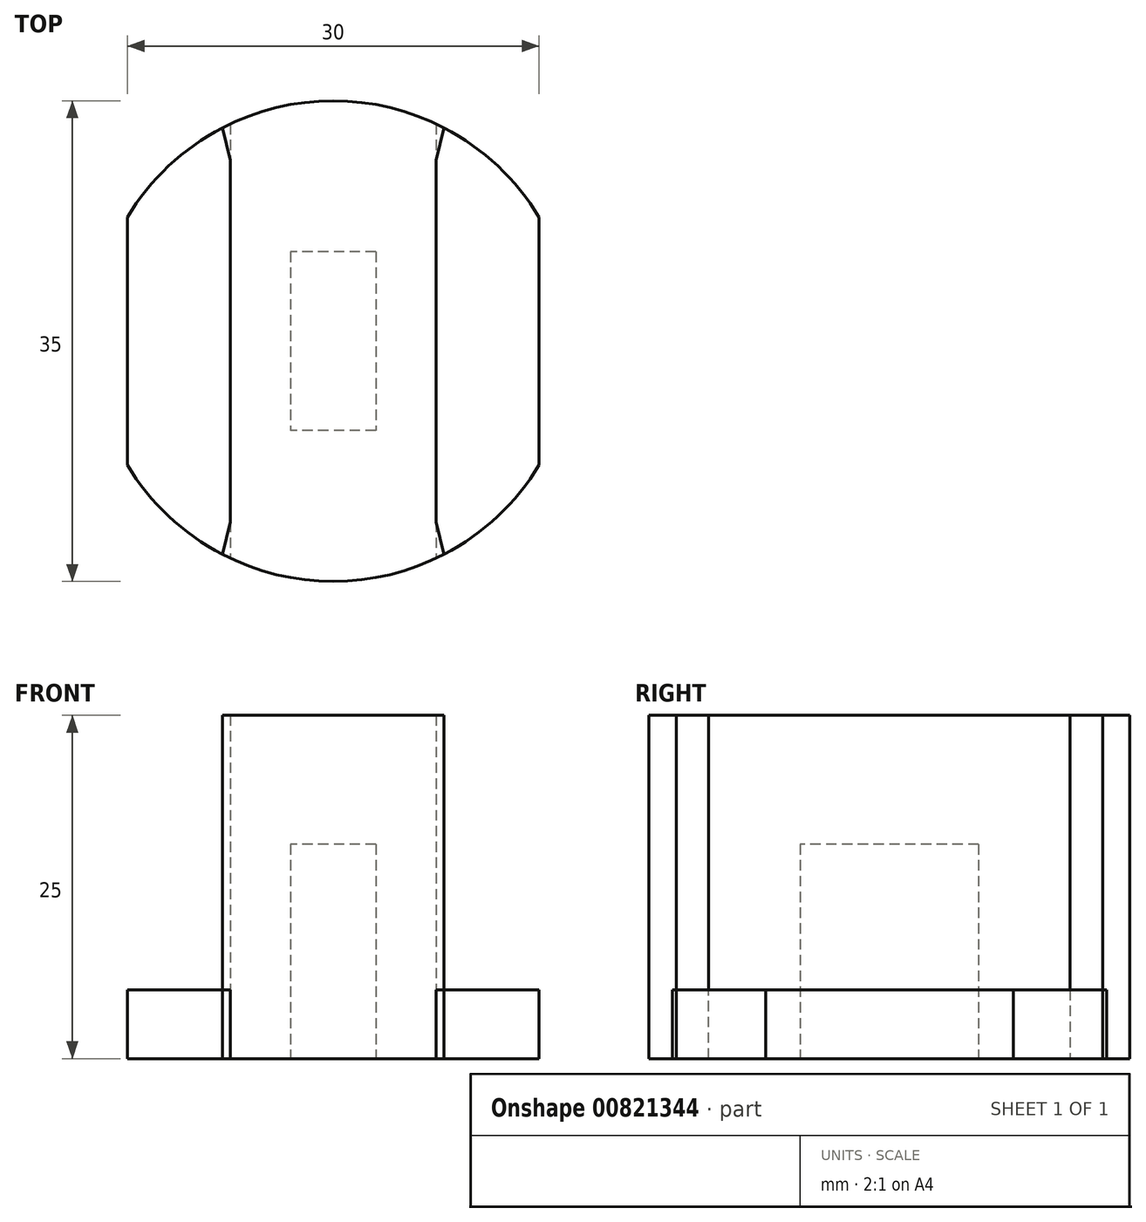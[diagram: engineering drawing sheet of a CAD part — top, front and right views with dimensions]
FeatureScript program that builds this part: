
annotation { "Feature Type Name" : "Feature", "Feature Type Description" : "" }
export const myFeature = defineFeature(function(context is Context, id is Id, definition is map)
    precondition{}
    {
        {
            var Q0;
            Q0=qCreatedBy(makeId("Top.planeOp"),FACE);
            var sketch = newSketch(context, id + "F0", { "sketchPlane" : qUnion([Q0])});
            skCircle(sketch, "E0", {"center": v(0, 0) * mm, "radius": 17.5 * mm});
            skLineSegment(sketch, "E1.bottom", {"start": v(7.5, 20) * mm, "end": v(-7.5, 20) * mm});
            skLineSegment(sketch, "E1.top", {"start": v(7.5, -20) * mm, "end": v(-7.5, -20) * mm});
            skLineSegment(sketch, "E1.left", {"start": v(7.5, 20) * mm, "end": v(7.5, -20) * mm});
            skLineSegment(sketch, "E1.right", {"start": v(-7.5, 20) * mm, "end": v(-7.5, -20) * mm});
            skLineSegment(sketch, "E2.bottom", {"start": v(3.1, 6.5) * mm, "end": v(-3.1, 6.5) * mm});
            skLineSegment(sketch, "E2.top", {"start": v(3.1, -6.5) * mm, "end": v(-3.1, -6.5) * mm});
            skLineSegment(sketch, "E2.left", {"start": v(3.1, 6.5) * mm, "end": v(3.1, -6.5) * mm});
            skLineSegment(sketch, "E2.right", {"start": v(-3.1, 6.5) * mm, "end": v(-3.1, -6.5) * mm});
            skLineSegment(sketch, "E3.bottom", {"start": v(15, 20) * mm, "end": v(-15, 20) * mm});
            skLineSegment(sketch, "E3.top", {"start": v(15, -20) * mm, "end": v(-15, -20) * mm});
            skLineSegment(sketch, "E3.left", {"start": v(15, 20) * mm, "end": v(15, -20) * mm});
            skLineSegment(sketch, "E3.right", {"start": v(-15, 20) * mm, "end": v(-15, -20) * mm});
            skLineSegment(sketch, "E4.bottom", {"start": v(23.86, 11.75) * mm, "end": v(-23.86, 11.75) * mm});
            skLineSegment(sketch, "E4.top", {"start": v(23.86, -11.75) * mm, "end": v(-23.86, -11.75) * mm});
            skLineSegment(sketch, "E4.left", {"start": v(23.86, 11.75) * mm, "end": v(23.86, -11.75) * mm});
            skLineSegment(sketch, "E4.right", {"start": v(-23.86, 11.75) * mm, "end": v(-23.86, -11.75) * mm});
            skSolve(sketch);
        }
        {
            var Q0;
            {var subQ0=sQuery(id+"F0.wireOp",EDGE,"E3.left");var subQ1=sQuery(id+"F0.wireOp",EDGE,"E0");var subQ2=makeQuery(id+"F0.imprint","INTERSECT",VERTEX,{"disambiguationData":[OD(0.0)],"derivedFrom":[subQ1,subQ0]});Q0=makeQuery(id+"F0.imprint","IMPRINT",FACE,{"disambiguationData":[TD([[makeQuery(id+"F0.imprint","IMPRINT",EDGE,{"disambiguationData":[TD([[subQ2,-1.0]])],"derivedFrom":subQ1}),1.0]])]});}
            var Q1;
            {var subQ0=sQuery(id+"F0.wireOp",EDGE,"E3.right");var subQ1=sQuery(id+"F0.wireOp",EDGE,"E0");var subQ2=makeQuery(id+"F0.imprint","INTERSECT",VERTEX,{"disambiguationData":[OD(0.0)],"derivedFrom":[subQ1,subQ0]});Q1=makeQuery(id+"F0.imprint","IMPRINT",FACE,{"disambiguationData":[TD([[makeQuery(id+"F0.imprint","IMPRINT",EDGE,{"disambiguationData":[TD([[subQ2,1.0]])],"derivedFrom":subQ1}),1.0]])]});}
            var Q2;
            {var subQ0=sQuery(id+"F0.wireOp",EDGE,"E1.right");var subQ1=sQuery(id+"F0.wireOp",EDGE,"E0");var subQ2=makeQuery(id+"F0.imprint","INTERSECT",VERTEX,{"disambiguationData":[OD(0.0)],"derivedFrom":[subQ1,subQ0]});Q2=makeQuery(id+"F0.imprint","IMPRINT",FACE,{"disambiguationData":[TD([[makeQuery(id+"F0.imprint","IMPRINT",EDGE,{"disambiguationData":[TD([[subQ2,-1.0]])],"derivedFrom":subQ1}),1.0]])]});}
            var Q3;
            {var subQ0=sQuery(id+"F0.wireOp",EDGE,"E1.left");var subQ1=sQuery(id+"F0.wireOp",EDGE,"E0");var subQ2=makeQuery(id+"F0.imprint","INTERSECT",VERTEX,{"disambiguationData":[OD(1.0)],"derivedFrom":[subQ1,subQ0]});Q3=makeQuery(id+"F0.imprint","IMPRINT",FACE,{"disambiguationData":[TD([[makeQuery(id+"F0.imprint","IMPRINT",EDGE,{"disambiguationData":[TD([[subQ2,-1.0]])],"derivedFrom":subQ1}),1.0]])]});}
            var Q4;
            {var subQ0=sQuery(id+"F0.wireOp",EDGE,"E4.top");var subQ1=sQuery(id+"F0.wireOp",EDGE,"E0");var subQ2=makeQuery(id+"F0.imprint","INTERSECT",VERTEX,{"disambiguationData":[OD(0.0)],"derivedFrom":[subQ1,subQ0]});Q4=makeQuery(id+"F0.imprint","IMPRINT",FACE,{"disambiguationData":[TD([[makeQuery(id+"F0.imprint","IMPRINT",EDGE,{"disambiguationData":[TD([[subQ2,-1.0]])],"derivedFrom":subQ1}),1.0]])]});}
            var Q5;
            {var subQ0=sQuery(id+"F0.wireOp",EDGE,"E4.bottom");var subQ1=sQuery(id+"F0.wireOp",EDGE,"E0");var subQ2=makeQuery(id+"F0.imprint","INTERSECT",VERTEX,{"disambiguationData":[OD(0.0)],"derivedFrom":[subQ1,subQ0]});Q5=makeQuery(id+"F0.imprint","IMPRINT",FACE,{"disambiguationData":[TD([[makeQuery(id+"F0.imprint","IMPRINT",EDGE,{"disambiguationData":[TD([[subQ2,-1.0]])],"derivedFrom":subQ1}),1.0]])]});}
            extrude(context, id + "F1", {"entities" : qUnion([Q0, Q1, Q2, Q3, Q4, Q5]), "depth" : 5 * mm, "offsetDistance" : 25 * mm});
        }
        {
            var Q0;
            Q0=makeQuery(id+"F0.imprint","IMPRINT",FACE,{"disambiguationData":[TD([[makeQuery(id+"F0.imprint","IMPRINT",EDGE,{"derivedFrom":sQuery(id+"F0.wireOp",EDGE,"E2.bottom")}),1.0]])]});
            var Q1;
            Q1=makeQuery(id+"F0.imprint","IMPRINT",FACE,{"disambiguationData":[TD([[makeQuery(id+"F0.imprint","IMPRINT",EDGE,{"derivedFrom":sQuery(id+"F0.wireOp",EDGE,"E2.bottom")}),-1.0]])]});
            var Q2;
            {var subQ0=sQuery(id+"F0.wireOp",EDGE,"E4.bottom");var subQ1=sQuery(id+"F0.wireOp",EDGE,"E1.right");var subQ2=makeQuery(id+"F0.imprint","INTERSECT",VERTEX,{"derivedFrom":[subQ1,subQ0]});Q2=makeQuery(id+"F0.imprint","IMPRINT",FACE,{"disambiguationData":[TD([[makeQuery(id+"F0.imprint","IMPRINT",EDGE,{"disambiguationData":[TD([[subQ2,-1.0]])],"derivedFrom":subQ1}),1.0]])]});}
            var Q3;
            {var subQ9=sQuery(id+"F0.wireOp",EDGE,"E2.top");Q3=makeQuery(id+"F0.imprint","IMPRINT",FACE,{"disambiguationData":[TD([[makeQuery(id+"F0.imprint","IMPRINT",EDGE,{"derivedFrom":subQ9}),1.0]])]});}
            var Q4;
            {var subQ0=sQuery(id+"F0.wireOp",EDGE,"E4.bottom");var subQ1=sQuery(id+"F0.wireOp",EDGE,"E1.left");var subQ2=makeQuery(id+"F0.imprint","INTERSECT",VERTEX,{"derivedFrom":[subQ1,subQ0]});Q4=makeQuery(id+"F0.imprint","IMPRINT",FACE,{"disambiguationData":[TD([[makeQuery(id+"F0.imprint","IMPRINT",EDGE,{"disambiguationData":[TD([[subQ2,-1.0]])],"derivedFrom":subQ1}),-1.0]])]});}
            var Q5;
            {var subQ0=sQuery(id+"F0.wireOp",EDGE,"E4.bottom");var subQ1=sQuery(id+"F0.wireOp",EDGE,"E2.left");var subQ2=makeQuery(id+"F0.imprint","INTERSECT",VERTEX,{"derivedFrom":[subQ1,subQ0]});Q5=makeQuery(id+"F0.imprint","IMPRINT",FACE,{"disambiguationData":[TD([[makeQuery(id+"F0.imprint","IMPRINT",EDGE,{"disambiguationData":[TD([[subQ2,-1.0]])],"derivedFrom":subQ1}),-1.0]])]});}
            var Q6;
            {var subQ0=sQuery(id+"F0.wireOp",EDGE,"E2.top");Q6=makeQuery(id+"F0.imprint","IMPRINT",FACE,{"disambiguationData":[TD([[makeQuery(id+"F0.imprint","IMPRINT",EDGE,{"derivedFrom":subQ0}),-1.0]])]});}
            var Q7;
            {var subQ0=sQuery(id+"F0.wireOp",EDGE,"E4.top");var subQ1=sQuery(id+"F0.wireOp",EDGE,"E0");var subQ2=makeQuery(id+"F0.imprint","INTERSECT",VERTEX,{"disambiguationData":[OD(0.0)],"derivedFrom":[subQ1,subQ0]});Q7=makeQuery(id+"F0.imprint","IMPRINT",FACE,{"disambiguationData":[TD([[makeQuery(id+"F0.imprint","IMPRINT",EDGE,{"disambiguationData":[TD([[subQ2,-1.0]])],"derivedFrom":subQ1}),1.0]])]});}
            var Q8;
            {var subQ0=sQuery(id+"F0.wireOp",EDGE,"E1.right");var subQ1=sQuery(id+"F0.wireOp",EDGE,"E0");var subQ2=makeQuery(id+"F0.imprint","INTERSECT",VERTEX,{"disambiguationData":[OD(0.0)],"derivedFrom":[subQ1,subQ0]});Q8=makeQuery(id+"F0.imprint","IMPRINT",FACE,{"disambiguationData":[TD([[makeQuery(id+"F0.imprint","IMPRINT",EDGE,{"disambiguationData":[TD([[subQ2,-1.0]])],"derivedFrom":subQ1}),1.0]])]});}
            var Q9;
            {var subQ0=sQuery(id+"F0.wireOp",EDGE,"E4.bottom");var subQ1=sQuery(id+"F0.wireOp",EDGE,"E0");var subQ2=makeQuery(id+"F0.imprint","INTERSECT",VERTEX,{"disambiguationData":[OD(0.0)],"derivedFrom":[subQ1,subQ0]});Q9=makeQuery(id+"F0.imprint","IMPRINT",FACE,{"disambiguationData":[TD([[makeQuery(id+"F0.imprint","IMPRINT",EDGE,{"disambiguationData":[TD([[subQ2,-1.0]])],"derivedFrom":subQ1}),1.0]])]});}
            var Q10;
            {var subQ0=sQuery(id+"F0.wireOp",EDGE,"E1.left");var subQ1=sQuery(id+"F0.wireOp",EDGE,"E0");var subQ2=makeQuery(id+"F0.imprint","INTERSECT",VERTEX,{"disambiguationData":[OD(1.0)],"derivedFrom":[subQ1,subQ0]});Q10=makeQuery(id+"F0.imprint","IMPRINT",FACE,{"disambiguationData":[TD([[makeQuery(id+"F0.imprint","IMPRINT",EDGE,{"disambiguationData":[TD([[subQ2,-1.0]])],"derivedFrom":subQ1}),1.0]])]});}
            var Q11;
            {var subQ0=sQuery(id+"F0.wireOp",EDGE,"E1.left");var subQ1=sQuery(id+"F0.wireOp",EDGE,"E0");var subQ2=makeQuery(id+"F0.imprint","INTERSECT",VERTEX,{"disambiguationData":[OD(0.0)],"derivedFrom":[subQ1,subQ0]});Q11=makeQuery(id+"F0.imprint","IMPRINT",FACE,{"disambiguationData":[TD([[makeQuery(id+"F0.imprint","IMPRINT",EDGE,{"disambiguationData":[TD([[subQ2,-1.0]])],"derivedFrom":subQ1}),1.0]])]});}
            var Q12;
            {var subQ0=sQuery(id+"F0.wireOp",EDGE,"E1.right");var subQ1=sQuery(id+"F0.wireOp",EDGE,"E0");var subQ2=makeQuery(id+"F0.imprint","INTERSECT",VERTEX,{"disambiguationData":[OD(1.0)],"derivedFrom":[subQ1,subQ0]});Q12=makeQuery(id+"F0.imprint","IMPRINT",FACE,{"disambiguationData":[TD([[makeQuery(id+"F0.imprint","IMPRINT",EDGE,{"disambiguationData":[TD([[subQ2,-1.0]])],"derivedFrom":subQ1}),1.0]])]});}
            extrude(context, id + "F2", {"entities" : qUnion([Q0, Q1, Q2, Q3, Q4, Q5, Q6, Q7, Q8, Q9, Q10, Q11, Q12]), "depth" : 25 * mm, "offsetDistance" : 25 * mm});
        }
        {
            var Q0;
            Q0=makeQuery(id+"F0.imprint","IMPRINT",FACE,{"disambiguationData":[TD([[makeQuery(id+"F0.imprint","IMPRINT",EDGE,{"derivedFrom":sQuery(id+"F0.wireOp",EDGE,"E2.bottom")}),1.0]])]});
            var Q1;
            {var subQ0=sQuery(id+"F0.wireOp",EDGE,"E4.bottom");var subQ1=sQuery(id+"F0.wireOp",EDGE,"E2.left");var subQ2=makeQuery(id+"F0.imprint","INTERSECT",VERTEX,{"derivedFrom":[subQ1,subQ0]});Q1=makeQuery(id+"F0.imprint","IMPRINT",FACE,{"disambiguationData":[TD([[makeQuery(id+"F0.imprint","IMPRINT",EDGE,{"disambiguationData":[TD([[subQ2,-1.0]])],"derivedFrom":subQ1}),-1.0]])]});}
            var Q2;
            {var subQ0=sQuery(id+"F0.wireOp",EDGE,"E2.top");Q2=makeQuery(id+"F0.imprint","IMPRINT",FACE,{"disambiguationData":[TD([[makeQuery(id+"F0.imprint","IMPRINT",EDGE,{"derivedFrom":subQ0}),-1.0]])]});}
            extrude(context, id + "F3", {"entities" : qUnion([Q0, Q1, Q2]), "operationType" : NewBodyOperationType.REMOVE, "oppositeDirection" : true, "depth" : -15.6 * mm, "offsetDistance" : 25 * mm});
        }
        {
            var Q0;
            {var subQ0=sQuery(id+"F0.wireOp",EDGE,"E4.top");var subQ1=sQuery(id+"F0.wireOp",EDGE,"E0");Q0=makeQuery(id+"F2.opExtrude","SWEPT_EDGE",EDGE,{"disambiguationData":[OSD([subQ1,subQ0]),TDD([makeQuery(id+"F0.imprint","INTERSECT",VERTEX,{"disambiguationData":[OD(0.0)],"derivedFrom":[subQ1,subQ0]})])]});}
            var Q1;
            {var subQ0=sQuery(id+"F0.wireOp",EDGE,"E4.top");var subQ1=sQuery(id+"F0.wireOp",EDGE,"E0");Q1=makeQuery(id+"F2.opExtrude","SWEPT_EDGE",EDGE,{"disambiguationData":[OSD([subQ1,subQ0]),TDD([makeQuery(id+"F0.imprint","INTERSECT",VERTEX,{"disambiguationData":[OD(1.0)],"derivedFrom":[subQ1,subQ0]})])]});}
            var Q2;
            {var subQ0=sQuery(id+"F0.wireOp",EDGE,"E4.bottom");var subQ1=sQuery(id+"F0.wireOp",EDGE,"E0");Q2=makeQuery(id+"F2.opExtrude","SWEPT_EDGE",EDGE,{"disambiguationData":[OSD([subQ1,subQ0]),TDD([makeQuery(id+"F0.imprint","INTERSECT",VERTEX,{"disambiguationData":[OD(0.0)],"derivedFrom":[subQ1,subQ0]})])]});}
            var Q3;
            {var subQ0=sQuery(id+"F0.wireOp",EDGE,"E4.bottom");var subQ1=sQuery(id+"F0.wireOp",EDGE,"E0");Q3=makeQuery(id+"F2.opExtrude","SWEPT_EDGE",EDGE,{"disambiguationData":[OSD([subQ1,subQ0]),TDD([makeQuery(id+"F0.imprint","INTERSECT",VERTEX,{"disambiguationData":[OD(1.0)],"derivedFrom":[subQ1,subQ0]})])]});}
            chamfer(context, id + "F4", {"entities" : qUnion([Q0, Q1, Q2, Q3]), "width" : 2 * mm, "tangentPropagation" : true});
        }
    });
